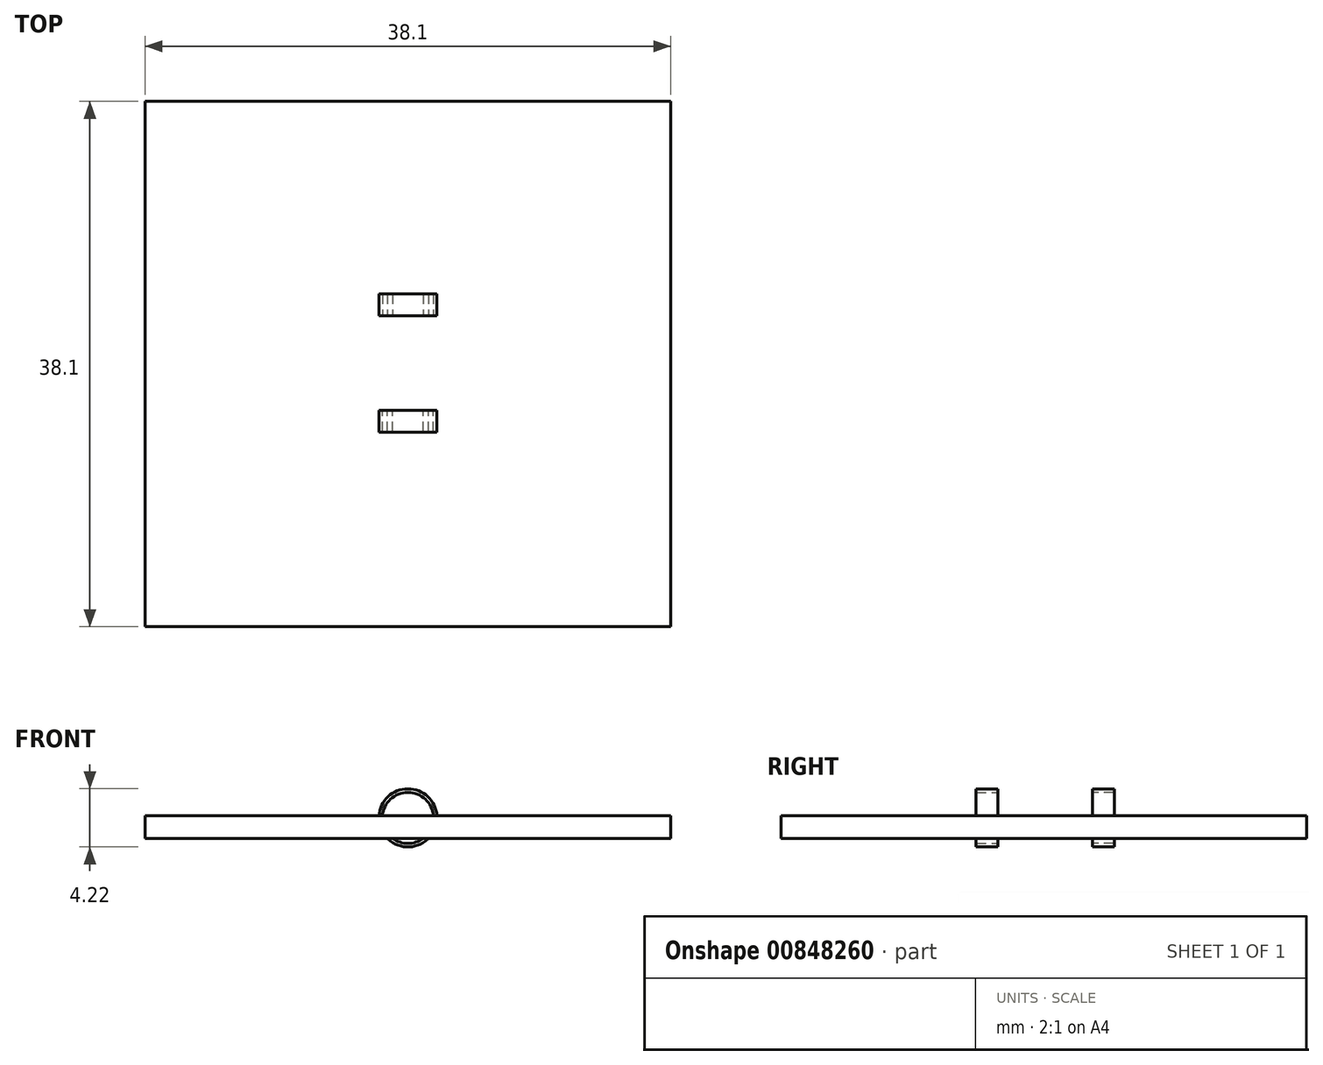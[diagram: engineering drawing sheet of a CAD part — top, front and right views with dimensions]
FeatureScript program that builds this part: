
annotation { "Feature Type Name" : "Feature", "Feature Type Description" : "" }
export const myFeature = defineFeature(function(context is Context, id is Id, definition is map)
    precondition{}
    {
        {
            var Q0;
            Q0=qCreatedBy(makeId("Front.planeOp"),FACE);
            var sketch = newSketch(context, id + "F0", { "sketchPlane" : qUnion([Q0])});
            skCircle(sketch, "E0", {"center": v(0, 0) * mm, "radius": 1.85 * mm});
            skCircle(sketch, "E1", {"center": v(0, 0) * mm, "radius": 2.1 * mm});
            skPoint(sketch, "E2", {"position": v(1.26, 1.7) * mm});
            skSolve(sketch);
        }
        {
            var Q0;
            Q0=makeQuery(id+"F0.imprint","IMPRINT",FACE,{"disambiguationData":[TD([[makeQuery(id+"F0.imprint","IMPRINT",EDGE,{"derivedFrom":sQuery(id+"F0.wireOp",EDGE,"E0")}),-1.0]])]});
            extrude(context, id + "F1", {"entities" : qUnion([Q0]), "oppositeDirection" : true, "depth" : 1.59 * mm, "offsetDistance" : 25.4 * mm});
        }
        {
            var Q0;
            Q0=makeQuery(id+"F1.opExtrude","CAP_FACE",FACE,{"disambiguationData":[OSD([sQuery(id+"F0.wireOp",EDGE,"E0"),sQuery(id+"F0.wireOp",EDGE,"E1")])],"isStart":true});
            cPlane(context, id + "F2", {"entities" : qUnion([Q0]), "cplaneType" : CPlaneType.OFFSET, "offset" : 6.86 * mm, "width" : 152.4 * mm, "height" : 152.4 * mm});
        }
        {
            var Q0;
            Q0=qCreatedBy(id+"F2.planeOp",FACE);
            var sketch = newSketch(context, id + "F3", { "sketchPlane" : qUnion([Q0])});
            skCircle(sketch, "E3", {"center": v(0, 0) * mm, "radius": 1.85 * mm});
            skCircle(sketch, "E4", {"center": v(0, 0) * mm, "radius": 2.1 * mm});
            skSolve(sketch);
        }
        {
            var Q0;
            Q0=makeQuery(id+"F3.imprint","IMPRINT",FACE,{"disambiguationData":[TD([[makeQuery(id+"F3.imprint","IMPRINT",EDGE,{"derivedFrom":sQuery(id+"F3.wireOp",EDGE,"E3")}),-1.0]])]});
            extrude(context, id + "F4", {"entities" : qUnion([Q0]), "depth" : 1.59 * mm, "offsetDistance" : 25.4 * mm});
        }
        {
            var Q0;
            Q0=qCreatedBy(makeId("Top.planeOp"),FACE);
            cPlane(context, id + "F5", {"entities" : qUnion([Q0]), "cplaneType" : CPlaneType.OFFSET, "offset" : ((.166 / 2) + (1 / 16)) * mm, "width" : 152.4 * mm, "height" : 152.4 * mm});
        }
        {
            var Q0;
            Q0=qCreatedBy(id+"F5.planeOp",FACE);
            var sketch = newSketch(context, id + "F6", { "sketchPlane" : qUnion([Q0])});
            skLineSegment(sketch, "E5.bottom", {"start": v(-19.05, 15.53) * mm, "end": v(19.05, 15.53) * mm});
            skLineSegment(sketch, "E5.top", {"start": v(-19.05, -22.57) * mm, "end": v(19.05, -22.57) * mm});
            skLineSegment(sketch, "E5.left", {"start": v(-19.05, 15.53) * mm, "end": v(-19.05, -22.57) * mm});
            skLineSegment(sketch, "E5.right", {"start": v(19.05, 15.53) * mm, "end": v(19.05, -22.57) * mm});
            skPoint(sketch, "E6", {"position": v(0, 15.53) * mm});
            skPoint(sketch, "E7", {"position": v(-19.05, -3.52) * mm});
            skSolve(sketch);
        }
        {
            var Q0;
            Q0=makeQuery(id+"F6.imprint","IMPRINT",FACE,{"disambiguationData":[TD([[makeQuery(id+"F6.imprint","IMPRINT",EDGE,{"derivedFrom":sQuery(id+"F6.wireOp",EDGE,"E5.bottom")}),-1.0]])]});
            extrude(context, id + "F7", {"entities" : qUnion([Q0]), "operationType" : NewBodyOperationType.ADD, "oppositeDirection" : true, "depth" : 1.63 * mm, "offsetDistance" : 25.4 * mm});
        }
    });
